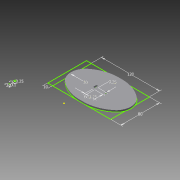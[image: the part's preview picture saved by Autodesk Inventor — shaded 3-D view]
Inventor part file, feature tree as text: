
AUTODESK INVENTOR PART (.ipt)
format: ipt  version: 2013 (Build 170138000, 138)  size: 103,424 bytes
history: native  units: mm
features: sketch x1, extrude x1
ambient origin geometry x8: Origin, YZ Plane, XZ Plane, XY Plane, X Axis, Y Axis, Z Axis, Center Point
feature tree (2):
  sketch  "Sketch1"  dims[d3=3.0mm d5=3.0mm d42=120.0mm d43=80.0mm d44=3.25mm d45=7.0mm d47=9.25mm d69=10.0mm d70=30.0mm d73=3.25mm d74=0.0mm]
  extrude  "Extrusion10"  Depth=3.0mm
